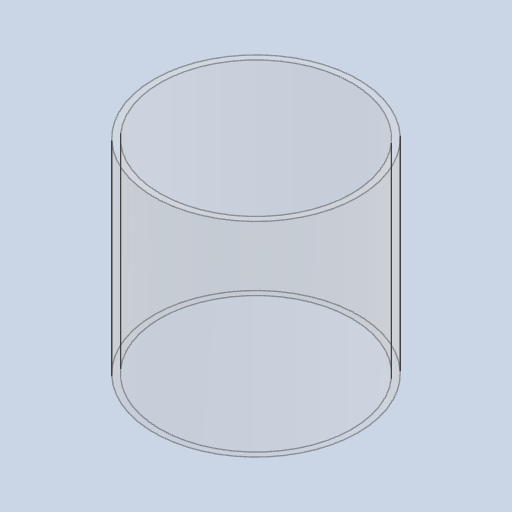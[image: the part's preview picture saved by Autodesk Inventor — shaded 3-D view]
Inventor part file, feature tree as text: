
AUTODESK INVENTOR PART (.ipt)
format: ipt  version: 2024.3 (Build 283343000, 343)  size: 147,456 bytes
history: native  units: mm
features: other x1, extrude x1, sketch x1
ambient origin geometry x8: Origin, YZ Plane, XZ Plane, XY Plane, X Axis, Y Axis, Z Axis, Center Point
bodies: Body1 (feature_tree)
feature tree (3):
  other  "Sólido1"
  extrude  "Extrusión1"  [1 undecoded]
  sketch  "Boceto1"  dims[d3=0.0mm]
note: 1 required parameter value undecoded (feature->parameter linkage not recoverable at this tier; creation-order binding heuristic only, values carry confidence <= 0.55)
